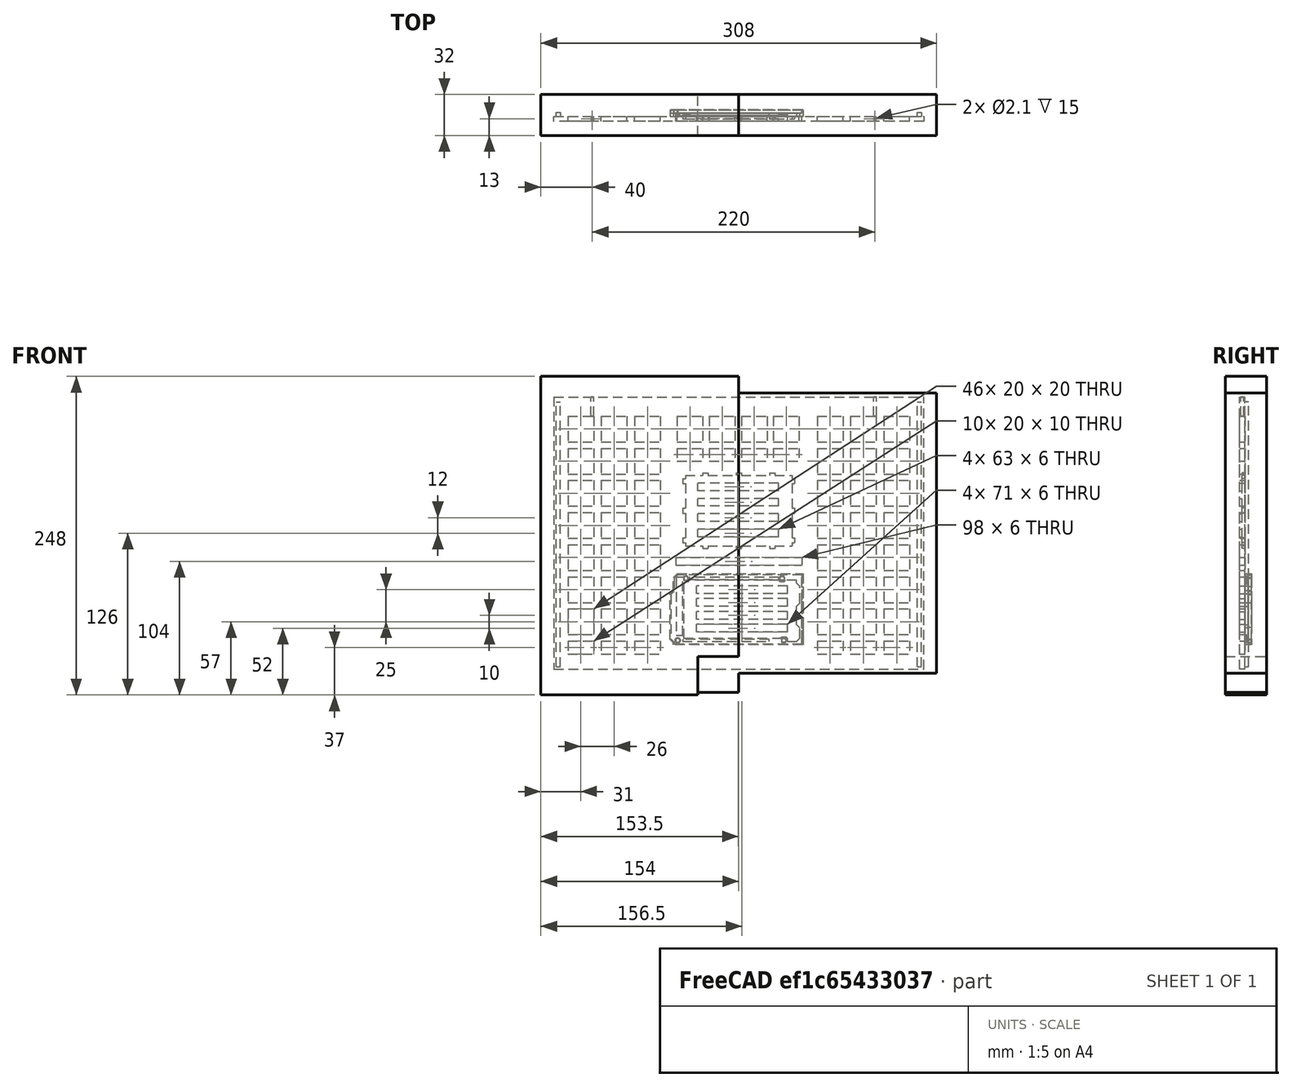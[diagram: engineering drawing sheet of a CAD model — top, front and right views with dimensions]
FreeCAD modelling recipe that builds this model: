
FCSTD DOCUMENT  (FreeCAD 0.17R13522 (Git))
Label: base_para_arduino_y_matrizia
License: CreativeCommons Attribution-ShareAlike
LicenseURL: http://creativecommons.org/licenses/by-sa/4.0/
objects: Part::Box×16, Part::Cut×14, Part::Feature×10, Part::Fuse×9, Part::FeaturePython×6
note: 55 computed .brp shape members not serialized (recipe doc carries the construction recipe); baked Part::Feature solids carry a one-line shape summary decoded from their .brp

FEATURE [Part::Feature] Cut001001001002003001008002002034001  label="base de la base con agujeros"
  shape: bbox 280 x 4 x 200 mm, 10 faces (baked)
FEATURE [Part::Box] Box  label="fleje apoyo lateral izquierdo"
  AttacherType = Attacher::AttachEngine3D
  Height = 200
  Length = 3
  Placement = pos=(2,0,-308) rot=(0,0,1;0rad)
  Width = 3
FEATURE [Part::Feature] Box001  label="fleje apoyo lateral derecho"
  Placement = pos=(283,0,-308) rot=(0,0,1;0rad)
  shape: bbox 3 x 3 x 200 mm, 6 faces (baked)
FEATURE [Part::Box] Box002  label="Cube"
  AttacherType = Attacher::AttachEngine3D
  Height = 200
  Length = 8
  Placement = pos=(280,-4,-308) rot=(0,0,1;0rad)
  Width = 4
FEATURE [Part::Fuse] Fusion
  Base = -> Cut001001001002003001008002002034001
  Refine = true
  Tool = -> Box002
FEATURE [Part::Fuse] Fusion001
  Base = -> Box001
  Refine = true
  Tool = -> Fusion
FEATURE [Part::Fuse] Fusion002
  Base = -> Box
  Refine = true
  Tool = -> Fusion001
FEATURE [Part::Box] Box003  label="Cube001"
  AttacherType = Attacher::AttachEngine3D
  Height = 10
  Length = 10
  Placement = pos=(-2,0,-112) rot=(0,0,1;0rad)
  Width = 10
FEATURE [Part::Feature] Box003001  label="Cube002"
  Placement = pos=(280,0,-112) rot=(0,0,1;0rad)
  shape: bbox 10 x 10 x 10 mm, 6 faces (baked)
FEATURE [Part::Cut] Cut
  Base = -> Fusion002
  Refine = true
  Tool = -> Box003
FEATURE [Part::Cut] Cut001001001002003001008002002034002  label="base sin soportes y sin recorte horizontal"
  Base = -> Cut
  Refine = true
  Tool = -> Box003001
FEATURE [Part::Feature] Fusion011001  label="cortador matrizia001"
  Placement = pos=(102.5,1,-224) rot=(1,0,0;1.5708rad)
  shape: bbox 87 x 3 x 59 mm, 54 faces (baked)
FEATURE [Part::Cut] Cut001001001002003001008002002034003
  Base = -> Cut001001001002003001008002002034002
  Refine = true
  Tool = -> Fusion011001
FEATURE [Part::Box] Box003002  label="Cube003"
  AttacherType = Attacher::AttachEngine3D
  Height = 200
  Length = 288
  Placement = pos=(0,-4,-508) rot=(0,0,1;0rad)
  Width = 4
FEATURE [Part::Feature] Box003003  label="fleje apoyo lateral izquierdo001"
  Placement = pos=(2,0,-506) rot=(0,0,1;0rad)
  shape: bbox 3 x 3 x 200 mm, 6 faces (baked)
FEATURE [Part::Feature] Box001001  label="fleje apoyo lateral derecho001"
  Placement = pos=(283,0,-507) rot=(0,0,1;0rad)
  shape: bbox 3 x 3 x 200 mm, 6 faces (baked)
FEATURE [Part::Fuse] Fusion011002
  Base = -> Cut001001001002003001008002002034003
  Refine = true
  Tool = -> Box003002
FEATURE [Part::Fuse] Fusion011003
  Base = -> Box003003
  Refine = true
  Tool = -> Fusion011002
FEATURE [Part::Fuse] Fusion011004
  Base = -> Box001001
  Refine = true
  Tool = -> Fusion011003
FEATURE [Part::Feature] Arduino_MEGA_Bumper_0003001_solid001001001  label="mega_bumper002"
  Placement = pos=(193,2.5,-300) rot=(0,0.707107,0.707107;3.14159rad)
  shape: bbox 103.5 x 5.08 x 55.22 mm, 538 faces (baked)
FEATURE [Part::Fuse] Fusion011005
  Base = -> Fusion011004
  Refine = true
  Tool = -> Arduino_MEGA_Bumper_0003001_solid001001001
FEATURE [Part::Box] Box003004  label="Cube004"
  AttacherType = Attacher::AttachEngine3D
  Height = 200
  Length = 300
  Placement = pos=(-5,-6,-520) rot=(0,0,1;0rad)
  Width = 10
FEATURE [Part::Cut] Cut001001001002003001008002002034004
  Base = -> Fusion011005
  Refine = true
  Tool = -> Box003004
FEATURE [Part::Box] Box003005  label="Cube005"
  AttacherType = Attacher::AttachEngine3D
  Height = 2
  Length = 300
  Placement = pos=(0,0,-320) rot=(0,0,1;0rad)
  Width = 18
FEATURE [Part::Cut] Cut001001001002003001008002002034005
  Base = -> Cut001001001002003001008002002034004
  Refine = true
  Tool = -> Box003005
FEATURE [Part::Box] Box003006  label="Cube006"
  AttacherType = Attacher::AttachEngine3D
  Height = 20
  Length = 20
  Placement = pos=(20,0,-150) rot=(0,0,1;0rad)
  Width = 30
FEATURE [Part::FeaturePython] Array  # Draft array (typed FeaturePython)
  Angle = 360
  ArrayType = 0
  Axis = (0,0,1)
  Base = -> Box003006
  Center = (0,0,0)
  Fuse = false
  IntervalAxis = (0,0,0)
  IntervalX = (26,0,0)
  IntervalY = (0,1,0)
  IntervalZ = (0,0,-25)
  NumberPolar = 1
  NumberX = 3
  NumberY = 1
  NumberZ = 7
  Placement = pos=(-9,-17,7) rot=(0,0,1;0rad)
FEATURE [Part::Feature] Array001
  Placement = pos=(185,-17,7) rot=(0,0,1;0rad)
  shape: bbox 72 x 30 x 170 mm, 126 faces, 21 solids (baked)
FEATURE [Part::Cut] Cut001001001002003001008002002034006
  Base = -> Cut001001001002003001008002002034005
  Refine = true
  Tool = -> Array001
FEATURE [Part::Cut] Cut001001001002003001008002002034007
  Base = -> Cut001001001002003001008002002034006
  Refine = true
  Tool = -> Array
FEATURE [Part::Box] Box003007  label="Cube007"
  AttacherType = Attacher::AttachEngine3D
  Height = 20
  Length = 20
  Placement = pos=(94,0,-143) rot=(0,0,1;0rad)
  Width = 33
FEATURE [Part::FeaturePython] Array002  # Draft array (typed FeaturePython)
  Angle = 360
  ArrayType = 0
  Axis = (0,0,1)
  Base = -> Box003007
  Center = (0,0,0)
  Fuse = false
  IntervalAxis = (0,0,0)
  IntervalX = (25,0,0)
  IntervalY = (0,1,0)
  IntervalZ = (0,0,0)
  NumberPolar = 1
  NumberX = 4
  NumberY = 1
  NumberZ = 1
  Placement = pos=(2,-23,0) rot=(0,0,1;0rad)
FEATURE [Part::Box] Box003008  label="Cube008"
  AttacherType = Attacher::AttachEngine3D
  Height = 10
  Length = 20
  Placement = pos=(96,0,-158) rot=(0,0,1;0rad)
  Width = 35
FEATURE [Part::FeaturePython] Array003  # Draft array (typed FeaturePython)
  Angle = 360
  ArrayType = 0
  Axis = (0,0,1)
  Base = -> Box003008
  Center = (0,0,0)
  Fuse = false
  IntervalAxis = (0,0,0)
  IntervalX = (25,0,0)
  IntervalY = (0,1,0)
  IntervalZ = (0,0,0)
  NumberPolar = 1
  NumberX = 4
  NumberY = 1
  NumberZ = 1
  Placement = pos=(0,-24,0) rot=(0,0,1;0rad)
FEATURE [Part::Cut] Cut001001001002003001008002002034008
  Base = -> Cut001001001002003001008002002034007
  Refine = true
  Tool = -> Array002
FEATURE [Part::Cut] Cut001001001002003001008002002034009
  Base = -> Cut001001001002003001008002002034008
  Placement = pos=(194,-17,0) rot=(0,0,1;0rad)
  Refine = true
  Tool = -> Array003
FEATURE [Part::Box] Box003009  label="Cube009"
  AttacherType = Attacher::AttachEngine3D
  Height = 10
  Length = 20
  Placement = pos=(11,-4,-308) rot=(0,0,1;0rad)
  Width = 32
FEATURE [Part::FeaturePython] Array004  # Draft array (typed FeaturePython)
  Angle = 360
  ArrayType = 0
  Axis = (0,0,1)
  Base = -> Box003009
  Center = (0,0,0)
  Fuse = false
  IntervalAxis = (0,0,0)
  IntervalX = (26,0,0)
  IntervalY = (0,1,0)
  IntervalZ = (0,0,0)
  NumberPolar = 1
  NumberX = 3
  NumberY = 1
  NumberZ = 1
  Placement = pos=(388,-28,0) rot=(0,0,1;0rad)
FEATURE [Part::Feature] Array004001  label="Array005"
  Placement = pos=(194,-28,0) rot=(0,0,1;0rad)
  shape: bbox 72 x 32 x 10 mm, 18 faces, 3 solids (baked)
FEATURE [Part::Cut] Cut001001001002003001008002002034010
  Base = -> Cut001001001002003001008002002034009
  Refine = true
  Tool = -> Array004
FEATURE [Part::Box] Box003010  label="Cube010"
  AttacherType = Attacher::AttachEngine3D
  Height = 6
  Length = 63
  Placement = pos=(306,0,-185) rot=(0,0,1;0rad)
  Width = 44
FEATURE [Part::FeaturePython] Array004002  # Draft array (typed FeaturePython)
  Angle = 360
  ArrayType = 0
  Axis = (0,0,1)
  Base = -> Box003010
  Center = (0,0,0)
  Fuse = false
  IntervalAxis = (0,0,0)
  IntervalX = (1,0,0)
  IntervalY = (0,1,0)
  IntervalZ = (0,0,-12)
  NumberPolar = 1
  NumberX = 1
  NumberY = 1
  NumberZ = 4
  Placement = pos=(0,-40,4) rot=(0,0,1;0rad)
FEATURE [Part::Cut] Cut001001001002003001008002002034011
  Base = -> Cut001001001002003001008002002034010
  Refine = true
  Tool = -> Array004002
FEATURE [Part::Box] Box003011  label="Cube011"
  AttacherType = Attacher::AttachEngine3D
  Height = 6
  Length = 71
  Placement = pos=(305,0,-263) rot=(0,0,1;0rad)
  Width = 43
FEATURE [Part::FeaturePython] Array004003  # Draft array (typed FeaturePython)
  Angle = 360
  ArrayType = 0
  Axis = (0,0,1)
  Base = -> Box003011
  Center = (0,0,0)
  Fuse = false
  IntervalAxis = (0,0,0)
  IntervalX = (1,0,0)
  IntervalY = (0,1,0)
  IntervalZ = (0,0,-10)
  NumberPolar = 1
  NumberX = 1
  NumberY = 1
  NumberZ = 4
  Placement = pos=(0,-36,2) rot=(0,0,1;0rad)
FEATURE [Part::Cut] Cut001001001002003001008002002034012
  Base = -> Cut001001001002003001008002002034011
  Refine = true
  Tool = -> Array004003
FEATURE [Part::Box] Box003012  label="Cube012"
  AttacherType = Attacher::AttachEngine3D
  Height = 6
  Length = 98
  Placement = pos=(289,-30,-239) rot=(0,0,1;0rad)
  Width = 35
FEATURE [Part::Cut] Cut001001001002003001008002002034013
  Base = -> Cut001001001002003001008002002034012
  Refine = true
  Tool = -> Box003012
FEATURE [Part::Cut] Cut001001001002003001008002002034014  label="base con aireadores"
  Base = -> Cut001001001002003001008002002034013
  Refine = true
  Tool = -> Array004001
FEATURE [Part::Box] Box003013  label="cortador derecha"
  AttacherType = Attacher::AttachEngine3D
  Height = 218
  Length = 154
  Placement = pos=(184,-32,-310) rot=(0,0,1;0rad)
  Width = 32
FEATURE [Part::Feature] Box003013001  label="cortador izquierda"
  Placement = pos=(338,-32,-323) rot=(0,0,1;0rad)
  shape: bbox 154 x 32 x 218 mm, 6 faces (baked)
FEATURE [Part::Box] Box003013002  label="cortador derecha fleje"
  AttacherType = Attacher::AttachEngine3D
  Height = 30
  Length = 122
  Placement = pos=(184,-32,-340) rot=(0,0,1;0rad)
  Width = 32
FEATURE [Part::Fuse] Fusion011006  label="Fusion cortador derecho"
  Base = -> Box003013
  Refine = true
  Tool = -> Box003013002
FEATURE [Part::Box] Box003013003  label="Cube013"
  AttacherType = Attacher::AttachEngine3D
  Height = 28
  Length = 32
  Placement = pos=(306,-32,-338) rot=(0,0,1;0rad)
  Width = 32
FEATURE [Part::Fuse] Fusion011007  label="Fusion cortador izquierda"
  Base = -> Box003013001
  Refine = true
  Tool = -> Box003013003
